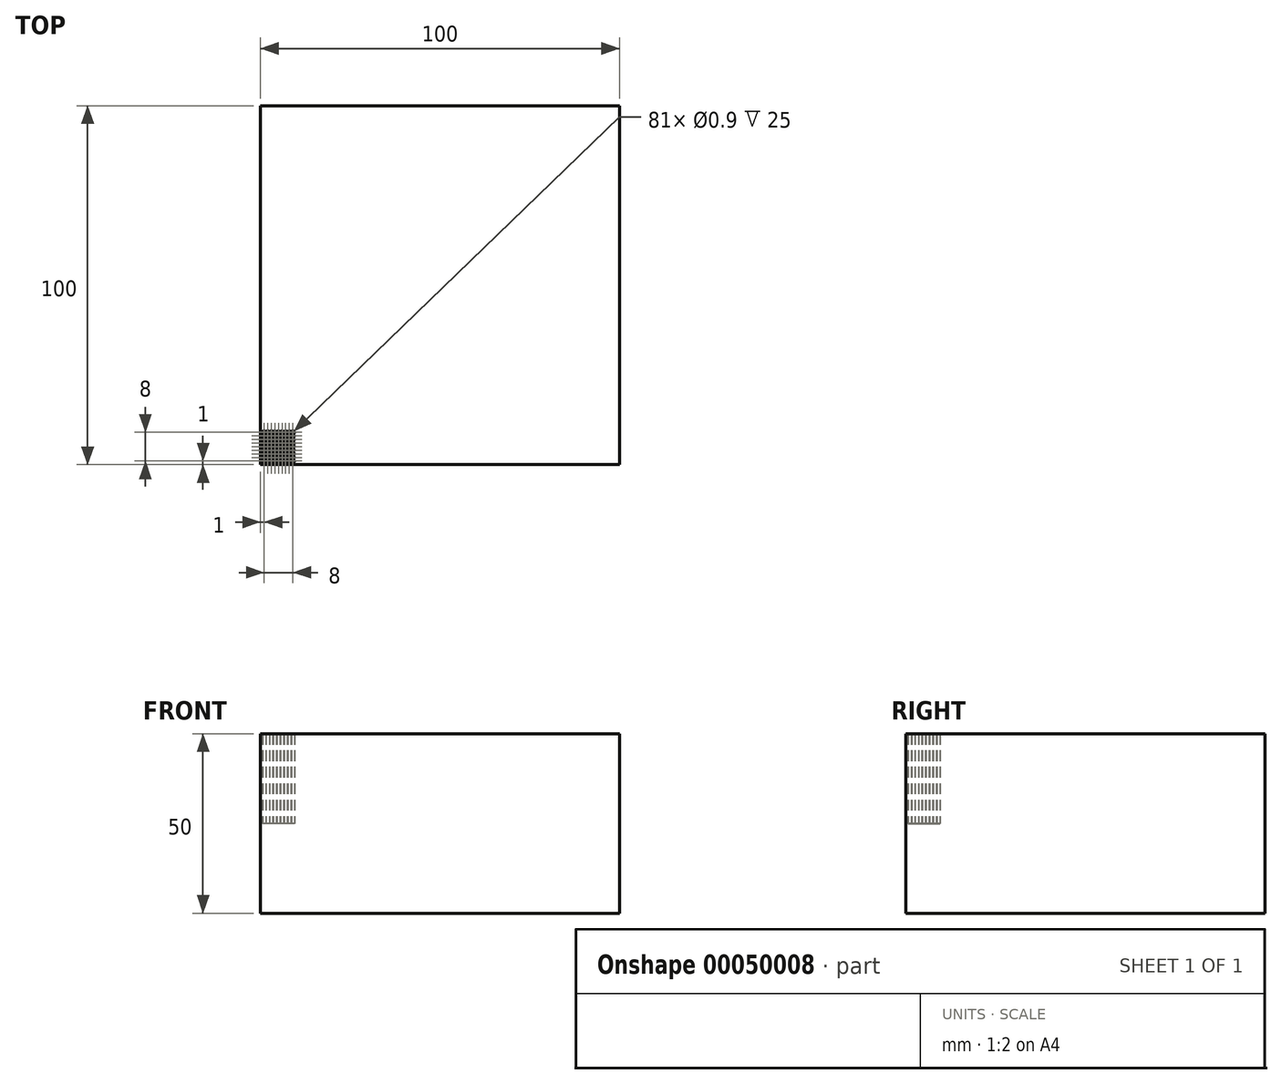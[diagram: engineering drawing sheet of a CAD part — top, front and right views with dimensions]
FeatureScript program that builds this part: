
annotation { "Feature Type Name" : "Feature", "Feature Type Description" : "" }
export const myFeature = defineFeature(function(context is Context, id is Id, definition is map)
    precondition{}
    {
        {
            var Q0;
            Q0=qCreatedBy(makeId("Top.planeOp"),FACE);
            var sketch = newSketch(context, id + "F0", { "sketchPlane" : qUnion([Q0])});
            skLineSegment(sketch, "E0.rect.bottom", {"start": v(50, -50) * mm, "end": v(-50, -50) * mm});
            skLineSegment(sketch, "E0.rect.top", {"start": v(50, 50) * mm, "end": v(-50, 50) * mm});
            skLineSegment(sketch, "E0.rect.left", {"start": v(50, -50) * mm, "end": v(50, 50) * mm});
            skLineSegment(sketch, "E0.rect.right", {"start": v(-50, -50) * mm, "end": v(-50, 50) * mm});
            skPoint(sketch, "E0.rect.middle", {"position": v(0, 0) * mm});
            skSolve(sketch);
        }
        {
            var Q0;
            Q0=makeQuery(id+"F0.imprint","IMPRINT",FACE,{"disambiguationData":[TD([[makeQuery(id+"F0.imprint","IMPRINT",EDGE,{"derivedFrom":sQuery(id+"F0.wireOp",EDGE,"E0.rect.bottom")}),-1.0]])]});
            extrude(context, id + "F1", {"entities" : qUnion([Q0]), "depth" : 25 * mm});
        }
        {
            var Q0;
            Q0=makeQuery(id+"F1.opExtrude","CAP_FACE",FACE,{"disambiguationData":[OSD([sQuery(id+"F0.wireOp",EDGE,"E0.rect.bottom"),sQuery(id+"F0.wireOp",EDGE,"E0.rect.top"),sQuery(id+"F0.wireOp",EDGE,"E0.rect.left"),sQuery(id+"F0.wireOp",EDGE,"E0.rect.right")])],"isStart":false});
            var sketch = newSketch(context, id + "F2", { "sketchPlane" : qUnion([Q0])});
            skCircle(sketch, "E1", {"center": v(-49, -49) * mm, "radius": 0.45 * mm});
            skCircle(sketch, "E2.0.1.0", {"center": v(-49, -48) * mm, "radius": 0.45 * mm});
            skCircle(sketch, "E2.0.2.0", {"center": v(-49, -47) * mm, "radius": 0.45 * mm});
            skCircle(sketch, "E2.0.3.0", {"center": v(-49, -46) * mm, "radius": 0.45 * mm});
            skCircle(sketch, "E2.0.4.0", {"center": v(-49, -45) * mm, "radius": 0.45 * mm});
            skCircle(sketch, "E2.0.5.0", {"center": v(-49, -44) * mm, "radius": 0.45 * mm});
            skCircle(sketch, "E2.0.6.0", {"center": v(-49, -43) * mm, "radius": 0.45 * mm});
            skCircle(sketch, "E2.0.7.0", {"center": v(-49, -42) * mm, "radius": 0.45 * mm});
            skCircle(sketch, "E2.0.8.0", {"center": v(-49, -41) * mm, "radius": 0.45 * mm});
            skCircle(sketch, "E2.1.0.0", {"center": v(-48, -49) * mm, "radius": 0.45 * mm});
            skCircle(sketch, "E2.1.1.0", {"center": v(-48, -48) * mm, "radius": 0.45 * mm});
            skCircle(sketch, "E2.1.2.0", {"center": v(-48, -47) * mm, "radius": 0.45 * mm});
            skCircle(sketch, "E2.1.3.0", {"center": v(-48, -46) * mm, "radius": 0.45 * mm});
            skCircle(sketch, "E2.1.4.0", {"center": v(-48, -45) * mm, "radius": 0.45 * mm});
            skCircle(sketch, "E2.1.5.0", {"center": v(-48, -44) * mm, "radius": 0.45 * mm});
            skCircle(sketch, "E2.1.6.0", {"center": v(-48, -43) * mm, "radius": 0.45 * mm});
            skCircle(sketch, "E2.1.7.0", {"center": v(-48, -42) * mm, "radius": 0.45 * mm});
            skCircle(sketch, "E2.1.8.0", {"center": v(-48, -41) * mm, "radius": 0.45 * mm});
            skCircle(sketch, "E2.2.0.0", {"center": v(-47, -49) * mm, "radius": 0.45 * mm});
            skCircle(sketch, "E2.2.1.0", {"center": v(-47, -48) * mm, "radius": 0.45 * mm});
            skCircle(sketch, "E2.2.2.0", {"center": v(-47, -47) * mm, "radius": 0.45 * mm});
            skCircle(sketch, "E2.2.3.0", {"center": v(-47, -46) * mm, "radius": 0.45 * mm});
            skCircle(sketch, "E2.2.4.0", {"center": v(-47, -45) * mm, "radius": 0.45 * mm});
            skCircle(sketch, "E2.2.5.0", {"center": v(-47, -44) * mm, "radius": 0.45 * mm});
            skCircle(sketch, "E2.2.6.0", {"center": v(-47, -43) * mm, "radius": 0.45 * mm});
            skCircle(sketch, "E2.2.7.0", {"center": v(-47, -42) * mm, "radius": 0.45 * mm});
            skCircle(sketch, "E2.2.8.0", {"center": v(-47, -41) * mm, "radius": 0.45 * mm});
            skCircle(sketch, "E2.3.0.0", {"center": v(-46, -49) * mm, "radius": 0.45 * mm});
            skCircle(sketch, "E2.3.1.0", {"center": v(-46, -48) * mm, "radius": 0.45 * mm});
            skCircle(sketch, "E2.3.2.0", {"center": v(-46, -47) * mm, "radius": 0.45 * mm});
            skCircle(sketch, "E2.3.3.0", {"center": v(-46, -46) * mm, "radius": 0.45 * mm});
            skCircle(sketch, "E2.3.4.0", {"center": v(-46, -45) * mm, "radius": 0.45 * mm});
            skCircle(sketch, "E2.3.5.0", {"center": v(-46, -44) * mm, "radius": 0.45 * mm});
            skCircle(sketch, "E2.3.6.0", {"center": v(-46, -43) * mm, "radius": 0.45 * mm});
            skCircle(sketch, "E2.3.7.0", {"center": v(-46, -42) * mm, "radius": 0.45 * mm});
            skCircle(sketch, "E2.3.8.0", {"center": v(-46, -41) * mm, "radius": 0.45 * mm});
            skCircle(sketch, "E2.4.0.0", {"center": v(-45, -49) * mm, "radius": 0.45 * mm});
            skCircle(sketch, "E2.4.1.0", {"center": v(-45, -48) * mm, "radius": 0.45 * mm});
            skCircle(sketch, "E2.4.2.0", {"center": v(-45, -47) * mm, "radius": 0.45 * mm});
            skCircle(sketch, "E2.4.3.0", {"center": v(-45, -46) * mm, "radius": 0.45 * mm});
            skCircle(sketch, "E2.4.4.0", {"center": v(-45, -45) * mm, "radius": 0.45 * mm});
            skCircle(sketch, "E2.4.5.0", {"center": v(-45, -44) * mm, "radius": 0.45 * mm});
            skCircle(sketch, "E2.4.6.0", {"center": v(-45, -43) * mm, "radius": 0.45 * mm});
            skCircle(sketch, "E2.4.7.0", {"center": v(-45, -42) * mm, "radius": 0.45 * mm});
            skCircle(sketch, "E2.4.8.0", {"center": v(-45, -41) * mm, "radius": 0.45 * mm});
            skCircle(sketch, "E2.5.0.0", {"center": v(-44, -49) * mm, "radius": 0.45 * mm});
            skCircle(sketch, "E2.5.1.0", {"center": v(-44, -48) * mm, "radius": 0.45 * mm});
            skCircle(sketch, "E2.5.2.0", {"center": v(-44, -47) * mm, "radius": 0.45 * mm});
            skCircle(sketch, "E2.5.3.0", {"center": v(-44, -46) * mm, "radius": 0.45 * mm});
            skCircle(sketch, "E2.5.4.0", {"center": v(-44, -45) * mm, "radius": 0.45 * mm});
            skCircle(sketch, "E2.5.5.0", {"center": v(-44, -44) * mm, "radius": 0.45 * mm});
            skCircle(sketch, "E2.5.6.0", {"center": v(-44, -43) * mm, "radius": 0.45 * mm});
            skCircle(sketch, "E2.5.7.0", {"center": v(-44, -42) * mm, "radius": 0.45 * mm});
            skCircle(sketch, "E2.5.8.0", {"center": v(-44, -41) * mm, "radius": 0.45 * mm});
            skCircle(sketch, "E2.6.0.0", {"center": v(-43, -49) * mm, "radius": 0.45 * mm});
            skCircle(sketch, "E2.6.1.0", {"center": v(-43, -48) * mm, "radius": 0.45 * mm});
            skCircle(sketch, "E2.6.2.0", {"center": v(-43, -47) * mm, "radius": 0.45 * mm});
            skCircle(sketch, "E2.6.3.0", {"center": v(-43, -46) * mm, "radius": 0.45 * mm});
            skCircle(sketch, "E2.6.4.0", {"center": v(-43, -45) * mm, "radius": 0.45 * mm});
            skCircle(sketch, "E2.6.5.0", {"center": v(-43, -44) * mm, "radius": 0.45 * mm});
            skCircle(sketch, "E2.6.6.0", {"center": v(-43, -43) * mm, "radius": 0.45 * mm});
            skCircle(sketch, "E2.6.7.0", {"center": v(-43, -42) * mm, "radius": 0.45 * mm});
            skCircle(sketch, "E2.6.8.0", {"center": v(-43, -41) * mm, "radius": 0.45 * mm});
            skCircle(sketch, "E2.7.0.0", {"center": v(-42, -49) * mm, "radius": 0.45 * mm});
            skCircle(sketch, "E2.7.1.0", {"center": v(-42, -48) * mm, "radius": 0.45 * mm});
            skCircle(sketch, "E2.7.2.0", {"center": v(-42, -47) * mm, "radius": 0.45 * mm});
            skCircle(sketch, "E2.7.3.0", {"center": v(-42, -46) * mm, "radius": 0.45 * mm});
            skCircle(sketch, "E2.7.4.0", {"center": v(-42, -45) * mm, "radius": 0.45 * mm});
            skCircle(sketch, "E2.7.5.0", {"center": v(-42, -44) * mm, "radius": 0.45 * mm});
            skCircle(sketch, "E2.7.6.0", {"center": v(-42, -43) * mm, "radius": 0.45 * mm});
            skCircle(sketch, "E2.7.7.0", {"center": v(-42, -42) * mm, "radius": 0.45 * mm});
            skCircle(sketch, "E2.7.8.0", {"center": v(-42, -41) * mm, "radius": 0.45 * mm});
            skCircle(sketch, "E2.8.0.0", {"center": v(-41, -49) * mm, "radius": 0.45 * mm});
            skCircle(sketch, "E2.8.1.0", {"center": v(-41, -48) * mm, "radius": 0.45 * mm});
            skCircle(sketch, "E2.8.2.0", {"center": v(-41, -47) * mm, "radius": 0.45 * mm});
            skCircle(sketch, "E2.8.3.0", {"center": v(-41, -46) * mm, "radius": 0.45 * mm});
            skCircle(sketch, "E2.8.4.0", {"center": v(-41, -45) * mm, "radius": 0.45 * mm});
            skCircle(sketch, "E2.8.5.0", {"center": v(-41, -44) * mm, "radius": 0.45 * mm});
            skCircle(sketch, "E2.8.6.0", {"center": v(-41, -43) * mm, "radius": 0.45 * mm});
            skCircle(sketch, "E2.8.7.0", {"center": v(-41, -42) * mm, "radius": 0.45 * mm});
            skCircle(sketch, "E2.8.8.0", {"center": v(-41, -41) * mm, "radius": 0.45 * mm});
            skLineSegment(sketch, "E2.direction1", {"start": v(-49, -49) * mm, "end": v(-48, -49) * mm, "construction": true});
            skLineSegment(sketch, "E2.direction2", {"start": v(-49, -49) * mm, "end": v(-49, -48) * mm, "construction": true});
            skSolve(sketch);
        }
        {
            var Q0;
            Q0=makeQuery(id+"F2.imprint","IMPRINT",FACE,{"disambiguationData":[TD([[makeQuery(id+"F2.imprint","IMPRINT",EDGE,{"derivedFrom":sQuery(id+"F2.wireOp",EDGE,"E1")}),-1.0]])]});
            extrude(context, id + "F3", {"entities" : qUnion([Q0]), "operationType" : NewBodyOperationType.ADD, "depth" : 25 * mm});
        }
    });
